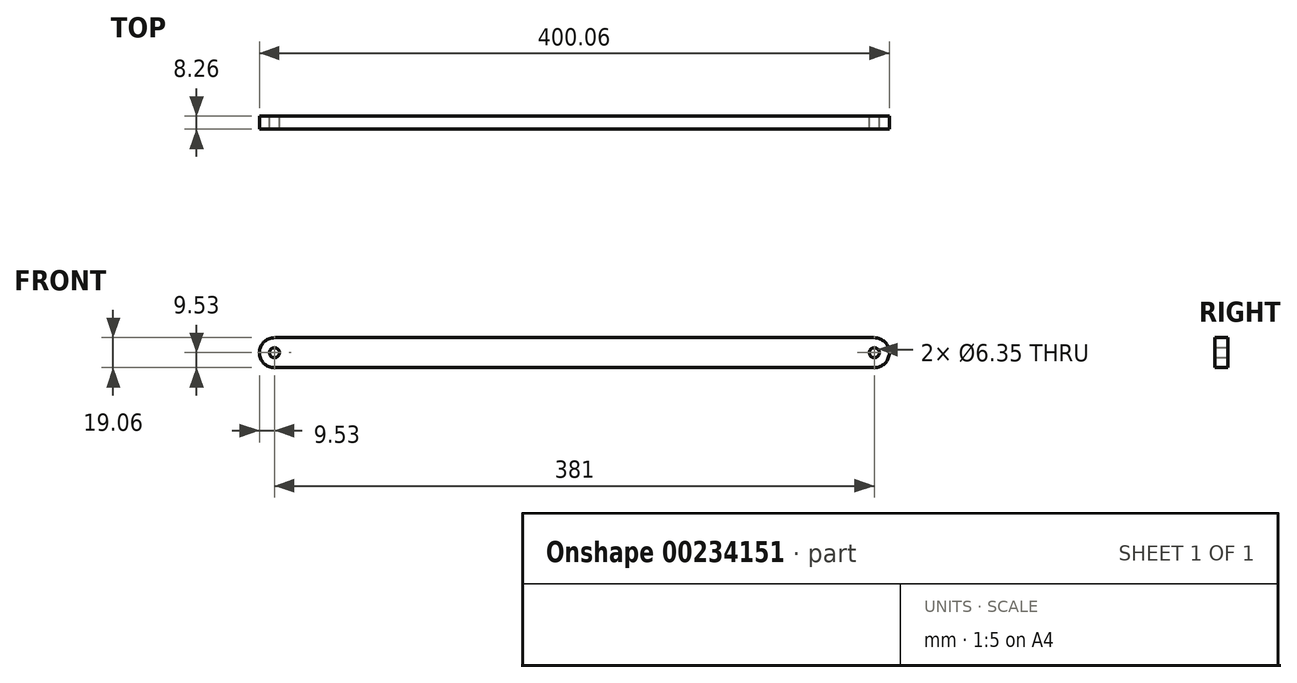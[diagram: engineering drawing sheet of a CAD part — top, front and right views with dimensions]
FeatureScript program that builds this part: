
annotation { "Feature Type Name" : "Feature", "Feature Type Description" : "" }
export const myFeature = defineFeature(function(context is Context, id is Id, definition is map)
    precondition{}
    {
        {
            var Q0;
            Q0=qCreatedBy(makeId("Front.planeOp"),FACE);
            var sketch = newSketch(context, id + "F0", { "sketchPlane" : qUnion([Q0])});
            skLineSegment(sketch, "E0.bottom", {"start": v(190.5, -9.53) * mm, "end": v(-190.5, -9.53) * mm});
            skLineSegment(sketch, "E0.top", {"start": v(190.5, 9.53) * mm, "end": v(-190.5, 9.53) * mm});
            skLineSegment(sketch, "E0.left", {"start": v(190.5, -9.53) * mm, "end": v(190.5, 9.53) * mm});
            skLineSegment(sketch, "E0.right", {"start": v(-190.5, -9.53) * mm, "end": v(-190.5, 9.52) * mm});
            skPoint(sketch, "E0.middle", {"position": v(0, 0) * mm});
            skCircle(sketch, "E1", {"center": v(-190.5, 0) * mm, "radius": 9.53 * mm});
            skCircle(sketch, "E2", {"center": v(190.5, 0) * mm, "radius": 9.53 * mm});
            skCircle(sketch, "E3", {"center": v(190.5, 0) * mm, "radius": 3.18 * mm});
            skCircle(sketch, "E4", {"center": v(-190.5, 0) * mm, "radius": 3.18 * mm});
            skSolve(sketch);
        }
        {
            var Q0;
            Q0 = qSketchRegion(id + "F0", true);
            extrude(context, id + "F1", {"entities" : qUnion([Q0]), "depth" : 8.25 * mm, "symmetric" : true});
        }
    });
